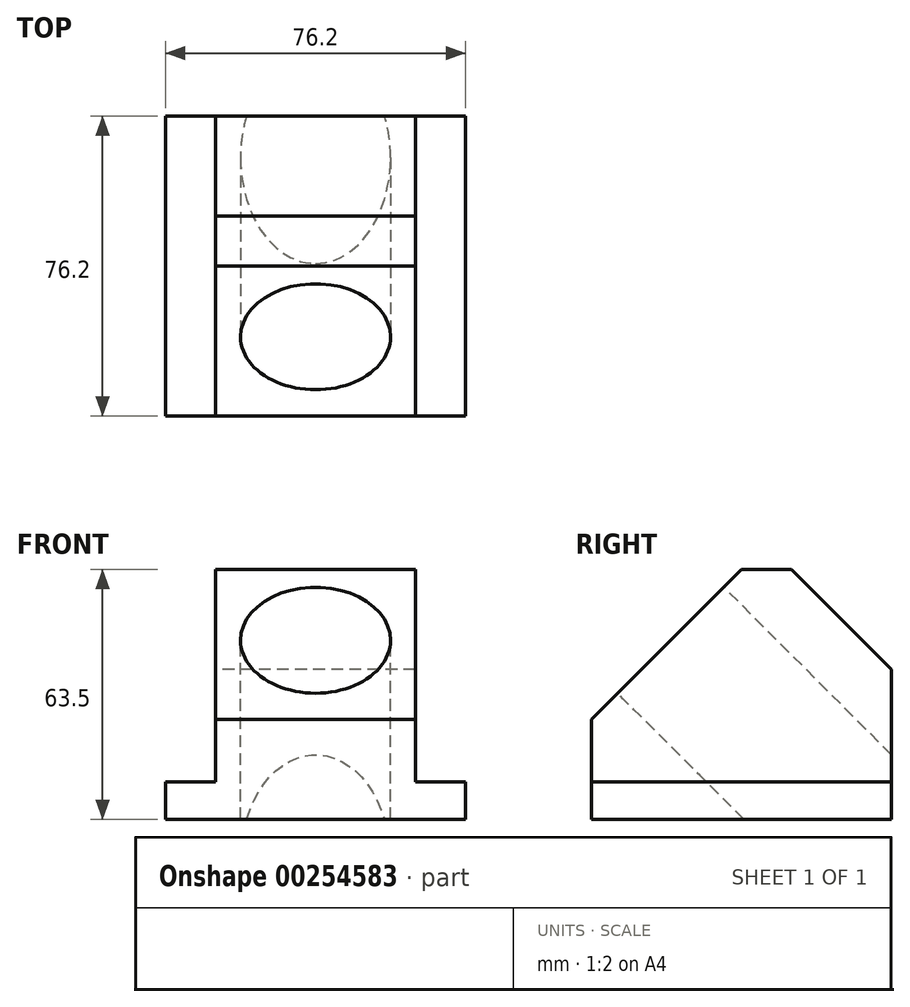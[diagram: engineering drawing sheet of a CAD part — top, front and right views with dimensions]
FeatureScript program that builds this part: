
annotation { "Feature Type Name" : "Feature", "Feature Type Description" : "" }
export const myFeature = defineFeature(function(context is Context, id is Id, definition is map)
    precondition{}
    {
        {
            var Q0;
            Q0=qCreatedBy(makeId("Top.planeOp"),FACE);
            var sketch = newSketch(context, id + "F0", { "sketchPlane" : qUnion([Q0])});
            skLineSegment(sketch, "E0.bottom", {"start": v(-38.1, 38.1) * mm, "end": v(0, 38.1) * mm});
            skLineSegment(sketch, "E0.left", {"start": v(-38.1, 38.1) * mm, "end": v(-38.1, 0) * mm});
            skLineSegment(sketch, "E1.MirrorCS", {"start": v(38.1, 38.1) * mm, "end": v(38.1, 0) * mm});
            skLineSegment(sketch, "E2.MirrorCS", {"start": v(38.1, 38.1) * mm, "end": v(0, 38.1) * mm});
            skLineSegment(sketch, "E3.MirrorCS", {"start": v(38.1, -38.1) * mm, "end": v(0, -38.1) * mm});
            skLineSegment(sketch, "E4.MirrorCS", {"start": v(-38.1, -38.1) * mm, "end": v(0, -38.1) * mm});
            skLineSegment(sketch, "E5.MirrorCS", {"start": v(-38.1, -38.1) * mm, "end": v(-38.1, 0) * mm});
            skLineSegment(sketch, "E6.MirrorCS", {"start": v(38.1, -38.1) * mm, "end": v(38.1, 0) * mm});
            skPoint(sketch, "E7.MirrorCS.end.orphan", {"position": v(0, 0) * mm});
            skSolve(sketch);
        }
        {
            var Q0;
            Q0=makeQuery(id+"F0.imprint","IMPRINT",FACE,{"disambiguationData":[TD([[makeQuery(id+"F0.imprint","IMPRINT",EDGE,{"derivedFrom":sQuery(id+"F0.wireOp",EDGE,"E0.bottom")}),-1.0]])]});
            extrude(context, id + "F1", {"entities" : qUnion([Q0]), "depth" : 9.52 * mm});
        }
        {
            var Q0;
            Q0=makeQuery(id+"F1.opExtrude","CAP_FACE",FACE,{"disambiguationData":[OSD([sQuery(id+"F0.wireOp",EDGE,"E0.bottom"),sQuery(id+"F0.wireOp",EDGE,"E0.left"),sQuery(id+"F0.wireOp",EDGE,"E1.MirrorCS"),sQuery(id+"F0.wireOp",EDGE,"E2.MirrorCS"),sQuery(id+"F0.wireOp",EDGE,"E3.MirrorCS"),sQuery(id+"F0.wireOp",EDGE,"E4.MirrorCS"),sQuery(id+"F0.wireOp",EDGE,"E5.MirrorCS"),sQuery(id+"F0.wireOp",EDGE,"E6.MirrorCS")])],"isStart":false});
            var sketch = newSketch(context, id + "F2", { "sketchPlane" : qUnion([Q0])});
            skLineSegment(sketch, "E8", {"start": v(-25.4, 38.1) * mm, "end": v(-25.4, -38.1) * mm});
            skLineSegment(sketch, "E9", {"start": v(25.4, 38.1) * mm, "end": v(25.4, -38.1) * mm});
            skSolve(sketch);
        }
        {
            var Q0;
            {var subQ0=sQuery(id+"F2.wireOp",EDGE,"E8");Q0=makeQuery(id+"F2.imprint","IMPRINT",FACE,{"disambiguationData":[TD([[makeQuery(id+"F2.imprint","IMPRINT",EDGE,{"derivedFrom":subQ0}),1.0]])]});}
            extrude(context, id + "F3", {"entities" : qUnion([Q0]), "operationType" : NewBodyOperationType.ADD, "depth" : 53.97 * mm});
        }
        {
            var Q0;
            Q0=makeQuery(id+"F3.opExtrude","SWEPT_FACE",FACE,{"disambiguationData":[OSD([sQuery(id+"F2.wireOp",EDGE,"E8")])]});
            var sketch = newSketch(context, id + "F4", { "sketchPlane" : qUnion([Q0])});
            skLineSegment(sketch, "E10", {"start": v(-38.1, 38.1) * mm, "end": v(-12.7, 63.5) * mm});
            skLineSegment(sketch, "E11", {"start": v(0, 63.5) * mm, "end": v(38.1, 25.4) * mm});
            skSolve(sketch);
        }
        {
            var Q0;
            {var subQ0=sQuery(id+"F4.wireOp",EDGE,"E10");Q0=makeQuery(id+"F4.imprint","IMPRINT",FACE,{"disambiguationData":[TD([[makeQuery(id+"F4.imprint","IMPRINT",EDGE,{"derivedFrom":subQ0}),1.0]])]});}
            var Q1;
            {var subQ0=sQuery(id+"F4.wireOp",EDGE,"E11");Q1=makeQuery(id+"F4.imprint","IMPRINT",FACE,{"disambiguationData":[TD([[makeQuery(id+"F4.imprint","IMPRINT",EDGE,{"derivedFrom":subQ0}),1.0]])]});}
            extrude(context, id + "F5", {"entities" : qUnion([Q0, Q1]), "operationType" : NewBodyOperationType.REMOVE, "oppositeDirection" : true, "depth" : 50.8 * mm});
        }
        {
            var Q0;
            Q0=makeQuery(id+"F5.boolean.opBoolean","COPY",FACE,{"derivedFrom":makeQuery(id+"F5.opExtrude","SWEPT_FACE",FACE,{"disambiguationData":[OSD([sQuery(id+"F4.wireOp",EDGE,"E11")])]})});
            var sketch = newSketch(context, id + "F6", { "sketchPlane" : qUnion([Q0])});
            skCircle(sketch, "E12", {"center": v(0, 19.5) * mm, "radius": 19.05 * mm});
            skSolve(sketch);
        }
        {
            var Q0;
            Q0=makeQuery(id+"F6.imprint","IMPRINT",FACE,{"disambiguationData":[TD([[makeQuery(id+"F6.imprint","IMPRINT",EDGE,{"derivedFrom":sQuery(id+"F6.wireOp",EDGE,"E12")}),1.0]])]});
            extrude(context, id + "F7", {"entities" : qUnion([Q0]), "operationType" : NewBodyOperationType.REMOVE, "oppositeDirection" : true, "depth" : 76.2 * mm});
        }
    });
